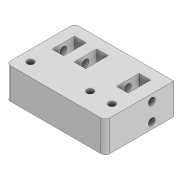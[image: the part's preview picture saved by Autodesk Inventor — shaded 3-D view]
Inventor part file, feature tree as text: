
AUTODESK INVENTOR PART (.ipt)
format: ipt  version: 2022 (Build 260153000, 153)  size: 183,296 bytes
history: native  units: mm
features: thicken_offset x3, extrude x2, fillet x1, sketch x1, projected_geometry x1
ambient origin geometry x8: Origin, YZ Plane, XZ Plane, XY Plane, X Axis, Y Axis, Z Axis, Center Point
bodies: Solid1 (feature_tree)
feature tree (8):
  extrude  "Extrusion1"  Depth=2.0mm
  fillet  "Fillet1"  Radius=25.0mm
  extrude  "Extrusion2"  Depth=2.0mm
  thicken_offset  "Thicken1"
  thicken_offset  "Thicken2"
  thicken_offset  "Thicken3"
  sketch  "Sketch2"  dims[d0=3.0mm d1=3.0mm d3=25.0mm d4=2.0mm d5=8.0mm d6=6.0mm d7=5.0mm d9=3.0mm d10=9.9mm d11=5.0mm d12=10.0mm d13=5.0mm d14=5.0mm d15=5.0mm d16=5.0mm d17=14.0mm d18=0.0mm d20=2.0mm d21=3.1mm d22=3.1mm d23=3.0mm d24=3.0mm d25=50.0mm d26=0.0mm d31=0.1mm d32=0.1mm d33=0.1mm d34=0.1mm d35=5.0mm d36=5.0mm d37=5.0mm d38=14.2mm d39=5.0mm d40=0.1mm d41=0.1mm]
  projected_geometry  "Projected Loop1"
